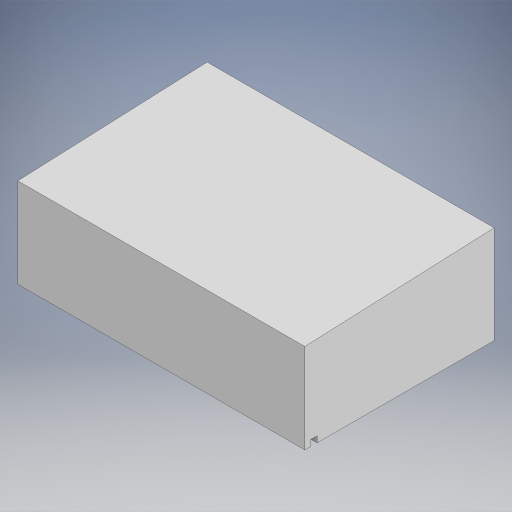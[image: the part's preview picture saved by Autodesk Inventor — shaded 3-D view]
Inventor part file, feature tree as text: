
AUTODESK INVENTOR PART (.ipt)
format: ipt  version: 2023.1 (Build 271208000, 208)  size: 197,120 bytes
history: native  units: in
note: dims shown in document units (in); Inventor stores cm internally (conversion verified against a paired STEP export)
features: extrude x1, sketch x1
ambient origin geometry x8: Origin, YZ Plane, XZ Plane, XY Plane, X Axis, Y Axis, Z Axis, Center Point
bodies: Solid1 (feature_tree)
feature tree (2):
  extrude  "Extrusion1"  Depth=11.625in
  sketch  "Sketch1"  dims[d0=6.0in d1=11.625in d2=0.5in d3=0.375in d4=0.375in d5=0.375in d6=17.625in d7=0.0in]
